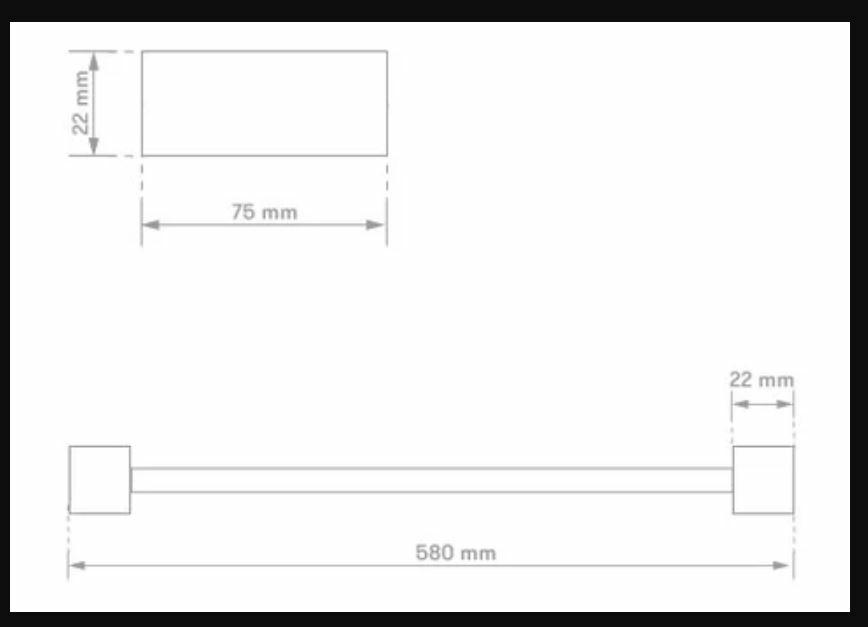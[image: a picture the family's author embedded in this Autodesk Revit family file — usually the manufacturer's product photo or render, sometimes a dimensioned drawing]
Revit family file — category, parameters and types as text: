
# Revit family: 01-2454-11 TOALLERO BARRA METALICO QUADRA
name_source: partatom
category: Plumbing Fixtures
revit_build: Autodesk Revit 2018 (Build: 20170223_1515(x64)
units: mm (PartAtom-declared; Revit-internal decimal feet)

## family parameters
Cut with Voids When Loaded = No
Host = Face
OmniClass Number = 23.31.11.00
Part Type = Normal
Room Calculation Point = No
Round Connector Dimension = Use Diameter
Shared = No

## types (1)
- 01-2454-11
    Alto = 22 mm
    Ancho = 580 mm
    CW Connection = Yes
    Date Modified = 01-2454-11
    Default Elevation = 0 mm  [stored 0 ft]
    Description = TOALLERO
    Finish = Metal Laton Cromado
    HW Connection = Yes
    Link Ficha Tecnica = http://infotecnica.gricol.com
    Manufacturer = Gricol
    Model = 01-2454-11
    Product Name = TOALLERO BARRA METALICO QUADRA
    Profundidad = 75 mm  [stored 0.246063 ft]
    Type Image = TOALLERO BARRA METALICO QUADRA.JPG
    URL = https://www.gricol.com
    Vent Connection = No
    Waste Connection = No

note: [stored X ft] marks values corroborated as IEEE doubles in the binary element streams (Revit-internal decimal feet)

## geometry (parser evidence)
native form markers: Blend x4, Sweep x5
no freeform markers — native parametric forms only
